FCSTD DOCUMENT  (FreeCAD 0.14R3692 (Git))
Label: Escornabot
License: The MIT License (MIT)
LicenseURL: http://opensource.org/licenses/MIT
objects: Part::Feature×46, Part::Mirroring×26, Sketcher::SketchObject×18, PartDesign::Pocket×14, App::DocumentObjectGroup×8, PartDesign::Pad×4, Part::Compound×4, Part::Fillet×2, PartDesign::Chamfer×2
note: 134 computed .brp shape members not serialized (recipe doc carries the construction recipe); baked Part::Feature solids carry a one-line shape summary decoded from their .brp

FEATURE [Sketcher::SketchObject] Sketch  label="UnderPlate_BaseSketch"
  sketch-geometry (25):
    g0: Circle CenterX=-37.5 CenterY=30 CenterZ=0 NormalX=0 NormalY=0 NormalZ=1 Radius=1.6
    g1: LineSegment StartX=-43.5 StartY=-45.5249 StartZ=0 EndX=-43.5 EndY=34.2012 EndZ=0
    g2: LineSegment StartX=-43.5 StartY=34.2012 StartZ=0 EndX=-19.3256 EndY=43 EndZ=0
    g3: LineSegment StartX=-19.3256 StartY=43 StartZ=0 EndX=19.3256 EndY=43 EndZ=0
    g4: LineSegment [constr] StartX=-37.5 StartY=30 StartZ=0 EndX=-39.5521 EndY=35.6382 EndZ=0
    g5: Circle CenterX=37.5 CenterY=30 CenterZ=0 NormalX=0 NormalY=0 NormalZ=1 Radius=1.6
    g6: Circle CenterX=-37.5 CenterY=-45 CenterZ=0 NormalX=0 NormalY=0 NormalZ=1 Radius=1.6
    g7: Circle CenterX=37.5 CenterY=-45 CenterZ=0 NormalX=0 NormalY=0 NormalZ=1 Radius=1.6
    g8: LineSegment [constr] StartX=-37.5 StartY=-45 StartZ=0 EndX=-43.4088 EndY=-46.0419 EndZ=0
    g9: LineSegment StartX=-37.556 StartY=-79.2349 StartZ=0 EndX=-43.5 EndY=-45.5249 EndZ=0
    g10: Circle CenterX=0 CenterY=0 CenterZ=0 NormalX=0 NormalY=0 NormalZ=1 Radius=9
    g11: LineSegment [constr] StartX=31.5 StartY=-74 StartZ=0 EndX=-31.5 EndY=-74 EndZ=0
    g12: LineSegment [constr] StartX=-31.5 StartY=-74 StartZ=0 EndX=-31.5 EndY=-16 EndZ=0
    g13: LineSegment [constr] StartX=-31.5 StartY=-16 StartZ=0 EndX=31.5 EndY=-16 EndZ=0
    g14: LineSegment [constr] StartX=31.5 StartY=-16 StartZ=0 EndX=31.5 EndY=-74 EndZ=0
    g15: LineSegment StartX=19.3256 StartY=43 StartZ=0 EndX=43.5 EndY=34.2012 EndZ=0
    g16: LineSegment StartX=43.5 StartY=34.2012 StartZ=0 EndX=43.5 EndY=-45.5249 EndZ=0
    g17: LineSegment StartX=43.5 StartY=-45.5249 StartZ=0 EndX=37.556 EndY=-79.2349 EndZ=0
    g18: LineSegment StartX=-37.556 StartY=-79.2349 StartZ=0 EndX=-19.3256 EndY=-92 EndZ=0
    g19: LineSegment StartX=-19.3256 StartY=-92 StartZ=0 EndX=19.3256 EndY=-92 EndZ=0
    g20: LineSegment StartX=37.556 StartY=-79.2349 StartZ=0 EndX=19.3256 EndY=-92 EndZ=0
    g21: LineSegment StartX=-31.5 StartY=-19 StartZ=0 EndX=31.5 EndY=-19 EndZ=0
    g22: LineSegment StartX=31.5 StartY=-19 StartZ=0 EndX=31.5 EndY=-71 EndZ=0
    g23: LineSegment StartX=31.5 StartY=-71 StartZ=0 EndX=-31.5 EndY=-71 EndZ=0
    g24: LineSegment StartX=-31.5 StartY=-71 StartZ=0 EndX=-31.5 EndY=-19 EndZ=0
  constraints (67):
    c: DistanceX(g-1,g0) = -37.5
    c: Radius(g0) = 1.6
    c: Coincident(g2,g1)
    c: Vertical(g1)
    c: DistanceX(g1,g0) = 6
    c: Coincident(g2,g3)
    c: Symmetric(g3,g2,g-2)
    c: Coincident(g4,g0)
    c: Distance(g4) = 6
    c: PointOnObject(g4,g2)
    c: Equal(g6,g7)
    c: Equal(g7,g5)
    c: Equal(g5,g0)
    c: Symmetric(g5,g0,g-2)
    c: Coincident(g8,g6)
    c: Distance(g8) = 6
    c: Coincident(g9,g1)
    c: PointOnObject(g8,g9)
    c: Radius(g10) = 9
    c: Coincident(g10,g-1)
    c: Coincident(g11,g12)
    c: Coincident(g12,g13)
    c: Coincident(g13,g14)
    c: Coincident(g14,g11)
    c: Horizontal(g11)
    c: Horizontal(g13)
    c: Vertical(g12)
    c: Vertical(g14)
    c: DistanceY(g14) = -58
    c: DistanceX(g13) = 63
    c: Angle(g9,g8) = 1.5708
    c: Angle(g4,g2) = 1.5708
    c: Angle(g2) = 0.349066
    c: Angle(g9) = 1.74533
    c: Symmetric(g12,g13,g-2)
    c: DistanceY(g-1,g13) = -16
    c: Symmetric(g15,g1,g-2)
    c: Coincident(g3,g15)
    c: Symmetric(g1,g16,g-2)
    c: Coincident(g16,g15)
    c: Symmetric(g17,g9,g-2)
    c: Coincident(g17,g16)
    c: Coincident(g9,g18)
    c: Angle(g18) = -0.610865
    c: Coincident(g19,g20)
    c: Coincident(g17,g20)
    c: Coincident(g18,g19)
    c: Symmetric(g19,g18,g-2)
    c: Equal(g19,g3)
    c: DistanceY(g11,g19) = -18
    c: Coincident(g21,g22)
    c: Coincident(g22,g23)
    c: Coincident(g23,g24)
    c: Coincident(g24,g21)
    c: Horizontal(g21)
    c: Horizontal(g23)
    c: Vertical(g22)
    c: Vertical(g24)
    c: PointOnObject(g21,g12)
    c: DistanceY(g23,g11) = -3
    c: DistanceY(g21,g12) = 3
    c: Symmetric(g21,g21,g-2)
    c: Symmetric(g7,g6,g-2)
    c: DistanceY(g0,g6) = -75
    c: DistanceY(g-1,g0) = 30
    c: DistanceX(g6,g1) = -6
    c: DistanceY(g-1,g2) = 43
FEATURE [PartDesign::Pad] Pad  label="UnderPlate_Base"
  Length = 3
  Length2 = 100
  Sketch = -> Sketch
  Type = 0
FEATURE [Sketcher::SketchObject] Sketch001  label="UnderPlate_BatteryRecessRearSketch"
  ExternalGeometry = -> [Pad]
  Placement = pos=(0,-19,0) rot=(1,0,0;1.5708rad)
  Support = -> Pad [Face11]
  sketch-geometry (4):
    g0: ArcOfCircle CenterX=-27.5 CenterY=5 CenterZ=0 NormalX=0 NormalY=0 NormalZ=1 Radius=4 StartAngle=1.5708 EndAngle=4.71239
    g1: ArcOfCircle CenterX=27.5 CenterY=5 CenterZ=0 NormalX=0 NormalY=0 NormalZ=1 Radius=4 StartAngle=4.71239 EndAngle=7.85398
    g2: LineSegment StartX=-27.5 StartY=1 StartZ=0 EndX=27.5 EndY=1 EndZ=0
    g3: LineSegment StartX=-27.5 StartY=9 StartZ=0 EndX=27.5 EndY=9 EndZ=0
  constraints (14):
    c: Tangent(g0,g2)
    c: Tangent(g0,g3)
    c: Tangent(g1,g2)
    c: Tangent(g1,g3)
    c: Coincident(g0,g3)
    c: Coincident(g0,g2)
    c: Coincident(g2,g1)
    c: Coincident(g3,g1)
    c: Horizontal(g2)
    c: Equal(g0,g1)
    c: Radius(g0) = 4
    c: DistanceX(g0,g-3) = -4
    c: Symmetric(g0,g1,g-2)
    c: DistanceY(g0,g-3) = -1
FEATURE [PartDesign::Pocket] Pocket  label="UnderPlate_BatteryRecessRear"
  Length = 3
  Sketch = -> Sketch001
  Type = 0
FEATURE [Sketcher::SketchObject] Sketch002  label="UnderPlate_BatteryRecessFrontSketch"
  ExternalGeometry = -> [Pocket]
  Placement = pos=(0,-71,0) rot=(0,0.707107,0.707107;3.14159rad)
  Support = -> Pocket [Face15]
  sketch-geometry (4):
    g0: ArcOfCircle CenterX=-27.5 CenterY=5 CenterZ=0 NormalX=0 NormalY=0 NormalZ=1 Radius=4 StartAngle=1.5708 EndAngle=4.71239
    g1: ArcOfCircle CenterX=27.5 CenterY=5 CenterZ=0 NormalX=0 NormalY=0 NormalZ=1 Radius=4 StartAngle=4.71239 EndAngle=7.85398
    g2: LineSegment StartX=-27.5 StartY=1 StartZ=0 EndX=27.5 EndY=1 EndZ=0
    g3: LineSegment StartX=-27.5 StartY=9 StartZ=0 EndX=27.5 EndY=9 EndZ=0
  constraints (13):
    c: Tangent(g0,g2)
    c: Tangent(g0,g3)
    c: Tangent(g1,g2)
    c: Tangent(g1,g3)
    c: Coincident(g0,g3)
    c: Coincident(g0,g2)
    c: Coincident(g2,g1)
    c: Coincident(g3,g1)
    c: Equal(g0,g1)
    c: Radius(g0) = 4
    c: Symmetric(g0,g1,g-2)
    c: DistanceY(g0,g-3) = -1
    c: DistanceX(g0,g-3) = -4
FEATURE [PartDesign::Pocket] Pocket001  label="UnderPlate_BatteryRecessFront"
  Length = 3
  Sketch = -> Sketch002
  Type = 0
FEATURE [Sketcher::SketchObject] Sketch003  label="UnderPlate_BallCasterCutOutSketch"
  ExternalGeometry = -> [Pocket001]
  Placement = pos=(0,0,3) rot=(0,0,1;0rad)
  Support = -> Pocket001 [Face5]
  sketch-geometry (14):
    g0: Circle CenterX=-15 CenterY=38 CenterZ=0 NormalX=0 NormalY=0 NormalZ=1 Radius=1.6
    g1: Circle CenterX=15 CenterY=38 CenterZ=0 NormalX=0 NormalY=0 NormalZ=1 Radius=1.6
    g2: LineSegment StartX=-10 StartY=43 StartZ=0 EndX=-10 EndY=38 EndZ=0
    g3: LineSegment StartX=-10 StartY=43 StartZ=0 EndX=10 EndY=43 EndZ=0
    g4: LineSegment StartX=10 StartY=43 StartZ=0 EndX=10 EndY=38 EndZ=0
    g5: ArcOfCircle CenterX=0 CenterY=38 CenterZ=0 NormalX=0 NormalY=0 NormalZ=1 Radius=10 StartAngle=3.14159 EndAngle=6.28319
    g6: ArcOfCircle CenterX=0 CenterY=-87 CenterZ=0 NormalX=0 NormalY=0 NormalZ=1 Radius=10 StartAngle=7.7e-11 EndAngle=3.14159
    g7: LineSegment StartX=10 StartY=-87 StartZ=0 EndX=10 EndY=-92 EndZ=0
    g8: LineSegment StartX=-10 StartY=-87 StartZ=0 EndX=-10 EndY=-92 EndZ=0
    g9: Circle CenterX=-15 CenterY=-87 CenterZ=0 NormalX=0 NormalY=0 NormalZ=1 Radius=1.6
    g10: Circle CenterX=15 CenterY=-87 CenterZ=0 NormalX=0 NormalY=0 NormalZ=1 Radius=1.6
    g11: LineSegment StartX=-10 StartY=-92 StartZ=0 EndX=10 EndY=-92 EndZ=0
    g12: LineSegment [constr] StartX=-15 StartY=38 StartZ=0 EndX=15 EndY=38 EndZ=0
    g13: LineSegment [constr] StartX=-15 StartY=-87 StartZ=0 EndX=15 EndY=-87 EndZ=0
  constraints (40):
    c: Radius(g0) = 1.6
    c: Equal(g0,g1)
    c: Symmetric(g1,g0,g-2)
    c: DistanceX(g1,g0) = -30
    c: Vertical(g2)
    c: Coincident(g3,g2)
    c: Vertical(g4)
    c: Coincident(g3,g4)
    c: Coincident(g5,g2)
    c: Coincident(g5,g4)
    c: Tangent(g4,g5)
    c: Tangent(g2,g5)
    c: Radius(g5) = 10
    c: PointOnObject(g5,g-2)
    c: PointOnObject(g6,g-2)
    c: Equal(g6,g5)
    c: Coincident(g6,g7)
    c: Vertical(g7)
    c: Tangent(g6,g7)
    c: Vertical(g8)
    c: Coincident(g6,g8)
    c: Tangent(g6,g8)
    c: Radius(g9) = 1.6
    c: Equal(g9,g10)
    c: Symmetric(g9,g10,g-2)
    c: DistanceX(g9,g10) = 30
    c: Coincident(g8,g11)
    c: Coincident(g7,g11)
    c: Coincident(g12,g1)
    c: Coincident(g12,g0)
    c: PointOnObject(g5,g12)
    c: Coincident(g13,g10)
    c: Coincident(g13,g9)
    c: PointOnObject(g6,g13)
    c: PointOnObject(g2,g-3)
    c: PointOnObject(g3,g-3)
    c: DistanceY(g0,g-3) = 5
    c: PointOnObject(g8,g-4)
    c: PointOnObject(g7,g-4)
    c: DistanceY(g9,g-4) = -5
FEATURE [PartDesign::Pocket] Pocket002  label="UnderPlate_BallCasterCutOut"
  Length = 5
  Sketch = -> Sketch003
  Type = 1
FEATURE [Sketcher::SketchObject] Sketch004  label="UnderPlate_MotorCutOutSketch"
  Placement = pos=(0,0,3) rot=(0,0,1;0rad)
  Support = -> Pocket002 [Face5]
  sketch-geometry (8):
    g0: LineSegment StartX=-43.5 StartY=9 StartZ=0 EndX=-23.5 EndY=9 EndZ=0
    g1: LineSegment StartX=-23.5 StartY=9 StartZ=0 EndX=-23.5 EndY=-9 EndZ=0
    g2: LineSegment StartX=-23.5 StartY=-9 StartZ=0 EndX=-43.5 EndY=-9 EndZ=0
    g3: LineSegment StartX=-43.5 StartY=-9 StartZ=0 EndX=-43.5 EndY=9 EndZ=0
    g4: LineSegment StartX=23.5 StartY=9 StartZ=0 EndX=43.5 EndY=9 EndZ=0
    g5: LineSegment StartX=43.5 StartY=9 StartZ=0 EndX=43.5 EndY=-9 EndZ=0
    g6: LineSegment StartX=43.5 StartY=-9 StartZ=0 EndX=23.5 EndY=-9 EndZ=0
    g7: LineSegment StartX=23.5 StartY=-9 StartZ=0 EndX=23.5 EndY=9 EndZ=0
  constraints (23):
    c: Coincident(g0,g1)
    c: Coincident(g1,g2)
    c: Coincident(g2,g3)
    c: Coincident(g3,g0)
    c: Horizontal(g0)
    c: Horizontal(g2)
    c: Vertical(g1)
    c: Vertical(g3)
    c: DistanceY(g1) = -18
    c: DistanceX(g2) = -20
    c: Symmetric(g0,g1,g-1)
    c: Coincident(g4,g5)
    c: Coincident(g5,g6)
    c: Coincident(g6,g7)
    c: Coincident(g7,g4)
    c: Horizontal(g4)
    c: Horizontal(g6)
    c: Vertical(g5)
    c: Vertical(g7)
    c: Equal(g2,g6)
    c: Equal(g7,g1)
    c: Symmetric(g1,g6,g-2)
    c: DistanceX(g0,g4) = 87
FEATURE [PartDesign::Pocket] Pocket003  label="UnderPlate_MotorCutOut"
  Length = 5
  Sketch = -> Sketch004
  Type = 1
FEATURE [Sketcher::SketchObject] Sketch005  label="UnderPlate_CutOutSketch"
  ExternalGeometry = -> [Pocket003]
  Placement = pos=(0,0,3) rot=(0,0,1;0rad)
  Support = -> Pocket003 [Face5]
  sketch-geometry (17):
    g0: LineSegment StartX=-31.5 StartY=32.1838 StartZ=0 EndX=-23.5 EndY=35.0956 EndZ=0
    g1: LineSegment StartX=-23.5 StartY=35.0956 StartZ=0 EndX=-23.5 EndY=15 EndZ=0
    g2: LineSegment StartX=-23.5 StartY=15 StartZ=0 EndX=-31.5 EndY=15 EndZ=0
    g3: LineSegment StartX=-31.5 StartY=15 StartZ=0 EndX=-31.5 EndY=32.1838 EndZ=0
    g4: LineSegment [constr] StartX=-31.5 StartY=32.1838 StartZ=0 EndX=-33.5521 EndY=37.822 EndZ=0
    g5: LineSegment StartX=23.5 StartY=35.0956 StartZ=0 EndX=31.5 EndY=32.1838 EndZ=0
    g6: LineSegment StartX=31.5 StartY=32.1838 StartZ=0 EndX=31.5 EndY=15 EndZ=0
    g7: LineSegment StartX=31.5 StartY=15 StartZ=0 EndX=23.5 EndY=15 EndZ=0
    g8: LineSegment StartX=23.5 StartY=15 StartZ=0 EndX=23.5 EndY=35.0956 EndZ=0
    g9: Circle [constr] CenterX=-15 CenterY=38 CenterZ=0 NormalX=0 NormalY=0 NormalZ=1 Radius=6.6
    g10: ArcOfCircle CenterX=0 CenterY=38 CenterZ=0 NormalX=0 NormalY=0 NormalZ=1 Radius=16 StartAngle=4.03512 EndAngle=5.38966
    g11: LineSegment StartX=-10.0267 StartY=25.5314 StartZ=0 EndX=-17.5 EndY=31.5411 EndZ=0
    g12: LineSegment StartX=10.0267 StartY=25.5314 StartZ=0 EndX=17.5 EndY=31.5411 EndZ=0
    g13: LineSegment StartX=-17.5 StartY=31.5411 StartZ=0 EndX=-17.5 EndY=15 EndZ=0
    g14: LineSegment StartX=-17.5 StartY=15 StartZ=0 EndX=17.5 EndY=15 EndZ=0
    g15: LineSegment StartX=17.5 StartY=15 StartZ=0 EndX=17.5 EndY=31.5411 EndZ=0
    g16: LineSegment [constr] StartX=-15 StartY=38 StartZ=0 EndX=0 EndY=38 EndZ=0
  constraints (48):
    c: Coincident(g0,g1)
    c: Coincident(g1,g2)
    c: Coincident(g2,g3)
    c: Coincident(g3,g0)
    c: Horizontal(g2)
    c: Vertical(g1)
    c: Vertical(g3)
    c: Coincident(g4,g0)
    c: Distance(g4) = 6
    c: DistanceX(g2) = -8
    c: DistanceY(g-1,g1) = 15
    c: Coincident(g5,g6)
    c: Coincident(g6,g7)
    c: Coincident(g7,g8)
    c: Coincident(g8,g5)
    c: Horizontal(g7)
    c: Vertical(g6)
    c: Vertical(g8)
    c: Symmetric(g7,g1,g-2)
    c: Symmetric(g5,g0,g-2)
    c: Symmetric(g5,g0,g-2)
    c: Radius(g9) = 6.6
    c: Coincident(g14,g15)
    c: Coincident(g12,g15)
    c: Coincident(g10,g12)
    c: Coincident(g10,g11)
    c: Coincident(g11,g13)
    c: Coincident(g13,g14)
    c: Tangent(g12,g10)
    c: Tangent(g11,g10)
    c: PointOnObject(g10,g-2)
    c: Symmetric(g13,g14,g-2)
    c: Vertical(g13)
    c: Vertical(g15)
    c: Tangent(g9,g11)
    c: DistanceX(g-1,g9) = -15
    c: DistanceX(g14) = 35
    c: DistanceY(g-1,g13) = 15
    c: Radius(g10) = 16
    c: Equal(g13,g15)
    c: Horizontal(g16)
    c: Coincident(g16,g10)
    c: Coincident(g16,g9)
    c: DistanceX(g1,g13) = 6
    c: PointOnObject(g4,g-3)
    c: Angle(g4,g-3) = 1.5708
    c: Parallel(g0,g-3)
    c: DistanceY(g-3,g9) = -5
FEATURE [PartDesign::Pocket] Pocket004  label="UnderPlate_CutOut"
  Length = 5
  Sketch = -> Sketch005
  Type = 1
FEATURE [Sketcher::SketchObject] Sketch007  label="UnderPlate_PenHolderScrewHolesSketch"
  Placement = pos=(0,0,3) rot=(0,0,1;0rad)
  Support = -> Pocket004 [Face5]
  sketch-geometry (2):
    g0: Circle CenterX=-16 CenterY=0 CenterZ=0 NormalX=0 NormalY=0 NormalZ=1 Radius=1.6
    g1: Circle CenterX=16 CenterY=0 CenterZ=0 NormalX=0 NormalY=0 NormalZ=1 Radius=1.6
  constraints (5):
    c: Radius(g0) = 1.6
    c: Symmetric(g0,g1,g-1)
    c: PointOnObject(g0,g-1)
    c: DistanceX(g0,g1) = 32
    c: Equal(g0,g1)
FEATURE [PartDesign::Pocket] Pocket006  label="UnderPlate_PenHolderScrewHoles"
  Length = 5
  Sketch = -> Sketch007
  Type = 1
FEATURE [Sketcher::SketchObject] Sketch010  label="MainPlate_BaseSketch"
  Placement = pos=(0,0,33) rot=(0,0,1;0rad)
  sketch-geometry (25):
    g0: Circle CenterX=-37.5 CenterY=30 CenterZ=0 NormalX=0 NormalY=0 NormalZ=1 Radius=1.6
    g1: LineSegment StartX=-40.6648 StartY=37.537 StartZ=0 EndX=-19.9572 EndY=30 EndZ=0
    g2: LineSegment StartX=-19.9572 StartY=30 StartZ=0 EndX=19.9572 EndY=30 EndZ=0
    g3: LineSegment [constr] StartX=-37.5 StartY=30 StartZ=0 EndX=-35.4479 EndY=35.6382 EndZ=0
    g4: Circle CenterX=37.5 CenterY=30 CenterZ=0 NormalX=0 NormalY=0 NormalZ=1 Radius=1.6
    g5: Circle CenterX=-37.5 CenterY=-45 CenterZ=0 NormalX=0 NormalY=0 NormalZ=1 Radius=1.6
    g6: Circle CenterX=37.5 CenterY=-45 CenterZ=0 NormalX=0 NormalY=0 NormalZ=1 Radius=1.6
    g7: Circle CenterX=0 CenterY=0 CenterZ=0 NormalX=0 NormalY=0 NormalZ=1 Radius=9
    g8: LineSegment StartX=19.9572 StartY=30 StartZ=0 EndX=40.6648 EndY=37.537 EndZ=0
    g9: LineSegment StartX=-42.8166 StartY=-49.45 StartZ=0 EndX=-19.9572 EndY=-57.7701 EndZ=0
    g10: LineSegment StartX=-19.9572 StartY=-57.7701 StartZ=0 EndX=19.9572 EndY=-57.7701 EndZ=0
    g11: LineSegment StartX=42.8166 StartY=-49.45 StartZ=0 EndX=19.9572 EndY=-57.7701 EndZ=0
    g12: LineSegment [constr] StartX=-37.5 StartY=-45 StartZ=0 EndX=-39.5521 EndY=-50.6382 EndZ=0
    g13: LineSegment StartX=-47.5 StartY=22.5 StartZ=0 EndX=-47.5 EndY=-22.5 EndZ=0
    g14: LineSegment StartX=47.5 StartY=22.5 StartZ=0 EndX=47.5 EndY=-22.5 EndZ=0
    g15: LineSegment [constr] StartX=-42.9622 StartY=32.4829 StartZ=0 EndX=-37.5 EndY=30 EndZ=0
    g16: LineSegment StartX=-40.6648 StartY=37.537 StartZ=0 EndX=-47.5 EndY=22.5 EndZ=0
    g17: LineSegment StartX=-47.5 StartY=-22.5 StartZ=0 EndX=-42.8166 EndY=-49.45 EndZ=0
    g18: LineSegment [constr] StartX=-37.5 StartY=-45 StartZ=0 EndX=-43.4114 EndY=-46.0273 EndZ=0
    g19: LineSegment [constr] StartX=-37.5 StartY=30 StartZ=0 EndX=37.5 EndY=30 EndZ=0
    g20: LineSegment [constr] StartX=37.5 StartY=30 StartZ=0 EndX=37.5 EndY=-45 EndZ=0
    g21: LineSegment [constr] StartX=37.5 StartY=-45 StartZ=0 EndX=-37.5 EndY=-45 EndZ=0
    g22: LineSegment [constr] StartX=-37.5 StartY=-45 StartZ=0 EndX=-37.5 EndY=30 EndZ=0
    g23: LineSegment StartX=40.6648 StartY=37.537 StartZ=0 EndX=47.5 EndY=22.5 EndZ=0
    g24: LineSegment StartX=47.5 StartY=-22.5 StartZ=0 EndX=42.8166 EndY=-49.45 EndZ=0
  constraints (63):
    c: Radius(g0) = 1.6
    c: Coincident(g1,g2)
    c: Symmetric(g2,g1,g-2)
    c: Coincident(g3,g0)
    c: Distance(g3) = 6
    c: PointOnObject(g3,g1)
    c: Radius(g7) = 9
    c: Coincident(g7,g-1)
    c: Angle(g3,g1) = 1.5708
    c: Angle(g1) = -0.349066
    c: Symmetric(g8,g1,g-2)
    c: Coincident(g2,g8)
    c: Symmetric(g11,g9,g-2)
    c: Coincident(g10,g11)
    c: Coincident(g9,g10)
    c: Symmetric(g10,g9,g-2)
    c: Coincident(g12,g5)
    c: PointOnObject(g12,g9)
    c: Symmetric(g13,g13,g-1)
    c: DistanceY(g13) = -45
    c: Symmetric(g13,g14,g-2)
    c: Symmetric(g14,g13,g-2)
    c: DistanceX(g14,g13) = -95
    c: Coincident(g15,g0)
    c: Coincident(g16,g13)
    c: Coincident(g16,g1)
    c: PointOnObject(g15,g16)
    c: Angle(g16,g15) = 1.5708
    c: Coincident(g17,g13)
    c: Coincident(g17,g9)
    c: PointOnObject(g18,g17)
    c: Coincident(g18,g5)
    c: Coincident(g19,g20)
    c: Coincident(g20,g21)
    c: Coincident(g21,g22)
    c: Coincident(g22,g19)
    c: Horizontal(g19)
    c: Horizontal(g21)
    c: Vertical(g20)
    c: Vertical(g22)
    c: Symmetric(g19,g19,g-2)
    c: DistanceX(g19) = 75
    c: DistanceY(g20) = -75
    c: DistanceY(g-1,g19) = 30
    c: Coincident(g14,g23)
    c: Coincident(g8,g23)
    c: Coincident(g11,g24)
    c: Coincident(g14,g24)
    c: Angle(g9,g12) = 1.5708
    c: Angle(g18,g17) = 1.5708
    c: Coincident(g4,g19)
    c: Coincident(g0,g19)
    c: Coincident(g5,g21)
    c: Coincident(g6,g20)
    c: Equal(g0,g4)
    c: Equal(g4,g6)
    c: Equal(g6,g5)
    c: Equal(g18,g12)
    c: Equal(g12,g15)
    c: Equal(g15,g3)
    c: Equal(g10,g2)
    c: Parallel(g9,g1)
    c: PointOnObject(g1,g19)
FEATURE [PartDesign::Pad] Pad002  label="MainPlate_Base"
  Length = 3
  Length2 = 100
  Placement = pos=(0,0,33) rot=(0,0,1;0rad)
  Sketch = -> Sketch010
  Type = 0
FEATURE [Sketcher::SketchObject] Sketch011  label="MainPlate_CutOutSketch"
  ExternalGeometry = -> [Pad002]
  Placement = pos=(0,0,36) rot=(0,0,1;0rad)
  Support = -> Pad002 [Face19]
  sketch-geometry (18):
    g0: LineSegment StartX=-23.5 StartY=5 StartZ=0 EndX=-23.5 EndY=24.9044 EndZ=0
    g1: LineSegment StartX=-23.5 StartY=24.9044 StartZ=0 EndX=-31.5 EndY=27.8162 EndZ=0
    g2: LineSegment StartX=-31.5 StartY=27.8162 StartZ=0 EndX=-31.5 EndY=5 EndZ=0
    g3: LineSegment StartX=-31.5 StartY=5 StartZ=0 EndX=-23.5 EndY=5 EndZ=0
    g4: LineSegment [constr] StartX=-31.5 StartY=27.8162 StartZ=0 EndX=-29.4479 EndY=33.4543 EndZ=0
    g5: LineSegment StartX=23.5 StartY=24.9044 StartZ=0 EndX=23.5 EndY=5 EndZ=0
    g6: LineSegment StartX=23.5 StartY=5 StartZ=0 EndX=31.5 EndY=5 EndZ=0
    g7: LineSegment StartX=31.5 StartY=5 StartZ=0 EndX=31.5 EndY=27.8162 EndZ=0
    g8: LineSegment StartX=31.5 StartY=27.8162 StartZ=0 EndX=23.5 EndY=24.9044 EndZ=0
    g9: LineSegment StartX=-31.5 StartY=-5 StartZ=0 EndX=-31.5 EndY=-47.1838 EndZ=0
    g10: LineSegment StartX=-31.5 StartY=-47.1838 StartZ=0 EndX=-23.5 EndY=-50.0956 EndZ=0
    g11: LineSegment StartX=-23.5 StartY=-50.0956 StartZ=0 EndX=-23.5 EndY=-5 EndZ=0
    g12: LineSegment StartX=-23.5 StartY=-5 StartZ=0 EndX=-31.5 EndY=-5 EndZ=0
    g13: LineSegment StartX=23.5 StartY=-5 StartZ=0 EndX=23.5 EndY=-50.0956 EndZ=0
    g14: LineSegment StartX=23.5 StartY=-50.0956 StartZ=0 EndX=31.5 EndY=-47.1838 EndZ=0
    g15: LineSegment StartX=31.5 StartY=-47.1838 StartZ=0 EndX=31.5 EndY=-5 EndZ=0
    g16: LineSegment StartX=31.5 StartY=-5 StartZ=0 EndX=23.5 EndY=-5 EndZ=0
    g17: LineSegment [constr] StartX=-31.5 StartY=-47.1838 StartZ=0 EndX=-33.5521 EndY=-52.822 EndZ=0
  constraints (48):
    c: Coincident(g0,g1)
    c: Coincident(g1,g2)
    c: Coincident(g2,g3)
    c: Coincident(g0,g3)
    c: Horizontal(g3)
    c: Vertical(g0)
    c: Vertical(g2)
    c: DistanceX(g3) = 8
    c: Coincident(g4,g1)
    c: Distance(g4) = 6
    c: DistanceY(g-1,g0) = 5
    c: Coincident(g5,g6)
    c: Coincident(g6,g7)
    c: Coincident(g7,g8)
    c: Coincident(g8,g5)
    c: Vertical(g5)
    c: Horizontal(g6)
    c: Coincident(g9,g10)
    c: Coincident(g10,g11)
    c: Coincident(g11,g12)
    c: Coincident(g12,g9)
    c: Vertical(g11)
    c: Horizontal(g12)
    c: Coincident(g13,g14)
    c: Coincident(g14,g15)
    c: Coincident(g13,g16)
    c: Coincident(g15,g16)
    c: Symmetric(g15,g9,g-2)
    c: Symmetric(g14,g9,g-2)
    c: Symmetric(g13,g10,g-2)
    c: Vertical(g13)
    c: Horizontal(g16)
    c: Vertical(g9)
    c: Vertical(g7)
    c: Symmetric(g1,g7,g-2)
    c: Symmetric(g5,g0,g-2)
    c: Symmetric(g2,g6,g-2)
    c: Symmetric(g9,g2,g-1)
    c: Coincident(g9,g17)
    c: Equal(g17,g4)
    c: Equal(g12,g3)
    c: PointOnObject(g17,g-4)
    c: PointOnObject(g4,g-3)
    c: Angle(g4,g-3) = 1.5708
    c: Angle(g17,g-4) = 1.5708
    c: Parallel(g-3,g1)
    c: Parallel(g10,g-4)
    c: DistanceX(g2,g6) = 63
FEATURE [PartDesign::Pocket] Pocket007002  label="MainPlate_CutOut"
  Length = 5
  Placement = pos=(0,0,33) rot=(0,0,1;0rad)
  Sketch = -> Sketch011
  Type = 1
FEATURE [Sketcher::SketchObject] Sketch012  label="MainPlate_BracketMountingScrewHolesSketch"
  Placement = pos=(0,0,36) rot=(0,0,1;0rad)
  Support = -> Pocket007002 [Face5]
  sketch-geometry (4):
    g0: Circle CenterX=-36.5 CenterY=17.5 CenterZ=0 NormalX=0 NormalY=0 NormalZ=1 Radius=1.6
    g1: Circle CenterX=-36.5 CenterY=-17.5 CenterZ=0 NormalX=0 NormalY=0 NormalZ=1 Radius=1.6
    g2: Circle CenterX=36.5 CenterY=17.5 CenterZ=0 NormalX=0 NormalY=0 NormalZ=1 Radius=1.6
    g3: Circle CenterX=36.5 CenterY=-17.5 CenterZ=0 NormalX=0 NormalY=0 NormalZ=1 Radius=1.6
  constraints (9):
    c: Radius(g0) = 1.6
    c: DistanceY(g-1,g0) = 17.5
    c: Equal(g3,g1)
    c: Equal(g1,g2)
    c: Equal(g2,g0)
    c: Symmetric(g2,g0,g-2)
    c: Symmetric(g0,g1,g-1)
    c: Symmetric(g1,g3,g-2)
    c: DistanceX(g0,g2) = 73
FEATURE [PartDesign::Pocket] Pocket007003  label="MainPlate_BracketMountingScrewHoles"
  Length = 5
  Placement = pos=(0,0,33) rot=(0,0,1;0rad)
  Sketch = -> Sketch012
  Type = 1
FEATURE [Part::Fillet] Fillet001  label="UnderPlate_RoundedCorners"
  Base = -> Pocket006
  Edges = 23 edges: [Edge1 r=6,Edge129 r=1,Edge130 r=1,Edge134 r=1,Edge136 r=1,Edge137 r=1,Edge138 r=1,Edge139 r=1,Edge140 r=1,Edge141 r=1,Edge142 r=1,Edge143 r=1,Edge144 r=1,Edge145 r=1,Edge147 r=1,Edge148 r=1,Edge152 r=6,Edge153 r=6,Edge156 r=1,Edge157 r=1,Edge162 r=1,Edge164 r=6,Edge166 r=1]
FEATURE [Sketcher::SketchObject] Sketch015  label="MainPlate_BracketMountingHeadHolesSketch"
  ExternalGeometry = -> [Pocket007003]
  Placement = pos=(0,0,36) rot=(0,0,1;0rad)
  Support = -> Pocket007003 [Face5]
  sketch-geometry (4):
    g0: Circle CenterX=-36.5 CenterY=17.5 CenterZ=0 NormalX=0 NormalY=0 NormalZ=1 Radius=2.95
    g1: Circle CenterX=36.5 CenterY=17.5 CenterZ=0 NormalX=0 NormalY=0 NormalZ=1 Radius=2.95
    g2: Circle CenterX=36.5 CenterY=-17.5 CenterZ=0 NormalX=0 NormalY=0 NormalZ=1 Radius=2.95
    g3: Circle CenterX=-36.5 CenterY=-17.5 CenterZ=0 NormalX=0 NormalY=0 NormalZ=1 Radius=2.95
  constraints (8):
    c: Radius(g0) = 2.95
    c: Equal(g0,g3)
    c: Equal(g3,g2)
    c: Equal(g2,g1)
    c: Symmetric(g0,g3,g-1)
    c: Symmetric(g0,g1,g-2)
    c: Symmetric(g0,g2,g-1)
    c: Coincident(g0,g-3)
FEATURE [PartDesign::Pocket] Pocket007004  label="MainPlate_BracketMountingHeadHoles"
  Length = 1
  Placement = pos=(0,0,33) rot=(0,0,1;0rad)
  Sketch = -> Sketch015
  Type = 0
FEATURE [Sketcher::SketchObject] Sketch016  label="MainPlate_ULN2003SpacerSketch"
  Placement = pos=(0,0,36) rot=(0,0,1;0rad)
  Support = -> Pocket007004 [Face5]
  sketch-geometry (10):
    g0: Circle CenterX=-12.875 CenterY=13.175 CenterZ=0 NormalX=0 NormalY=0 NormalZ=1 Radius=2.4
    g1: Circle CenterX=-43.125 CenterY=-13.175 CenterZ=0 NormalX=0 NormalY=0 NormalZ=1 Radius=2.4
    g2: Circle CenterX=-12.875 CenterY=-13.175 CenterZ=0 NormalX=0 NormalY=0 NormalZ=1 Radius=2.4
    g3: LineSegment [constr] StartX=-28 StartY=15.75 StartZ=0 EndX=-28 EndY=0 EndZ=0
    g4: LineSegment [constr] StartX=-28 StartY=0 StartZ=0 EndX=-45.55 EndY=0 EndZ=0
    g5: Circle CenterX=-43.125 CenterY=13.175 CenterZ=0 NormalX=0 NormalY=0 NormalZ=1 Radius=2.4
    g6: Circle CenterX=12.875 CenterY=13.175 CenterZ=0 NormalX=0 NormalY=0 NormalZ=1 Radius=2.4
    g7: Circle CenterX=12.875 CenterY=-13.175 CenterZ=0 NormalX=0 NormalY=0 NormalZ=1 Radius=2.4
    g8: Circle CenterX=43.125 CenterY=13.175 CenterZ=0 NormalX=0 NormalY=0 NormalZ=1 Radius=2.4
    g9: Circle CenterX=43.125 CenterY=-13.175 CenterZ=0 NormalX=0 NormalY=0 NormalZ=1 Radius=2.4
  constraints (24):
    c: Coincident(g3,g4)
    c: Horizontal(g4)
    c: Vertical(g3)
    c: DistanceX(g4) = -17.55
    c: DistanceY(g3) = -15.75
    c: DistanceX(g5,g3) = 15.125
    c: DistanceY(g5,g3) = -13.175
    c: Radius(g5) = 2.4
    c: Symmetric(g5,g0,g3)
    c: Symmetric(g1,g5,g4)
    c: Symmetric(g5,g2,g3)
    c: Equal(g5,g0)
    c: Equal(g0,g2)
    c: Equal(g2,g1)
    c: DistanceX(g-1,g3) = -28
    c: Symmetric(g6,g0,g-2)
    c: Symmetric(g8,g5,g-2)
    c: Symmetric(g9,g1,g-2)
    c: Symmetric(g7,g2,g-2)
    c: Equal(g7,g9)
    c: Equal(g9,g8)
    c: Equal(g8,g6)
    c: Equal(g6,g5)
    c: PointOnObject(g3,g-1)
FEATURE [PartDesign::Pad] Pad003  label="MainPlate_ULN2003Spacer"
  Length = 5
  Length2 = 100
  Placement = pos=(0,0,33) rot=(0,0,1;0rad)
  Sketch = -> Sketch016
  Type = 0
FEATURE [PartDesign::Chamfer] Chamfer  label="MainPlate_ULN2003SpacerChamfer"
  Base = -> Pad003 [Edge86,Edge89,Edge87,Edge83,Edge88,Edge84,Edge90,Edge85]
  Placement = pos=(0,0,33) rot=(0,0,1;0rad)
  Size = 1
FEATURE [Sketcher::SketchObject] Sketch017  label="MainPlate_ULN2003ScrewHolesSketch"
  ExternalGeometry = -> [Chamfer]
  Placement = pos=(0,0,36) rot=(0,0,1;0rad)
  Support = -> Chamfer [Face1]
  sketch-geometry (8):
    g0: Circle CenterX=-43.125 CenterY=13.175 CenterZ=0 NormalX=0 NormalY=0 NormalZ=1 Radius=1.4
    g1: Circle CenterX=-43.125 CenterY=-13.175 CenterZ=0 NormalX=0 NormalY=0 NormalZ=1 Radius=1.4
    g2: Circle CenterX=-12.875 CenterY=-13.175 CenterZ=0 NormalX=0 NormalY=0 NormalZ=1 Radius=1.4
    g3: Circle CenterX=12.875 CenterY=13.175 CenterZ=0 NormalX=0 NormalY=0 NormalZ=1 Radius=1.4
    g4: Circle CenterX=12.875 CenterY=-13.175 CenterZ=0 NormalX=0 NormalY=0 NormalZ=1 Radius=1.4
    g5: Circle CenterX=43.125 CenterY=13.175 CenterZ=0 NormalX=0 NormalY=0 NormalZ=1 Radius=1.4
    g6: Circle CenterX=43.125 CenterY=-13.175 CenterZ=0 NormalX=0 NormalY=0 NormalZ=1 Radius=1.4
    g7: Circle CenterX=-12.875 CenterY=13.175 CenterZ=0 NormalX=0 NormalY=0 NormalZ=1 Radius=1.4
  constraints (16):
    c: Coincident(g-3,g0)
    c: Symmetric(g1,g0,g-1)
    c: Symmetric(g2,g4,g-2)
    c: Symmetric(g1,g6,g-2)
    c: Symmetric(g5,g0,g-2)
    c: Radius(g0) = 1.4
    c: Coincident(g7,g-4)
    c: Equal(g0,g1)
    c: Equal(g1,g2)
    c: Equal(g2,g4)
    c: Equal(g4,g5)
    c: Equal(g5,g6)
    c: Equal(g6,g3)
    c: Equal(g3,g7)
    c: Symmetric(g2,g7,g-1)
    c: Symmetric(g7,g3,g-2)
FEATURE [PartDesign::Pocket] Pocket007005  label="MainPlate_ULN2003ScrewHoles"
  Length = 5
  Midplane = true
  Placement = pos=(0,0,33) rot=(0,0,1;0rad)
  Sketch = -> Sketch017
  Type = 1
FEATURE [Sketcher::SketchObject] Sketch013  label="MainPlate_BreadBoardOutSketch"
  ExternalGeometry = -> [Pocket007005]
  Placement = pos=(0,0,36) rot=(0,0,1;0rad)
  Support = -> Pocket007005 [Face2]
  sketch-geometry (4):
    g0: LineSegment StartX=-18.25 StartY=-17 StartZ=0 EndX=18.25 EndY=-17 EndZ=0
    g1: LineSegment StartX=18.25 StartY=-17 StartZ=0 EndX=18.25 EndY=-57.7701 EndZ=0
    g2: LineSegment StartX=18.25 StartY=-57.7701 StartZ=0 EndX=-18.25 EndY=-57.7701 EndZ=0
    g3: LineSegment StartX=-18.25 StartY=-57.7701 StartZ=0 EndX=-18.25 EndY=-17 EndZ=0
  constraints (12):
    c: Coincident(g0,g1)
    c: Coincident(g1,g2)
    c: Coincident(g2,g3)
    c: Coincident(g3,g0)
    c: Horizontal(g0)
    c: Horizontal(g2)
    c: Vertical(g1)
    c: Vertical(g3)
    c: DistanceX(g2) = -36.5
    c: Symmetric(g1,g2,g-2)
    c: DistanceY(g-1,g0) = -17
    c: PointOnObject(g2,g-3)
FEATURE [PartDesign::Pad] Pad004  label="MainPlate_BreadBoardOut"
  Length = 2
  Length2 = 100
  Placement = pos=(0,0,33) rot=(0,0,1;0rad)
  Sketch = -> Sketch013
  Type = 0
FEATURE [Sketcher::SketchObject] Sketch014  label="MainPlate_BreadBoardInSketch"
  Placement = pos=(0,0,36) rot=(0,0,1;0rad)
  Support = -> Pad004 [Face2]
  sketch-geometry (4):
    g0: LineSegment StartX=-17.25 StartY=-18 StartZ=0 EndX=17.25 EndY=-18 EndZ=0
    g1: LineSegment StartX=17.25 StartY=-18 StartZ=0 EndX=17.25 EndY=-63.5 EndZ=0
    g2: LineSegment StartX=17.25 StartY=-63.5 StartZ=0 EndX=-17.25 EndY=-63.5 EndZ=0
    g3: LineSegment StartX=-17.25 StartY=-63.5 StartZ=0 EndX=-17.25 EndY=-18 EndZ=0
  constraints (12):
    c: Coincident(g2,g3)
    c: Coincident(g1,g2)
    c: Coincident(g0,g3)
    c: Coincident(g0,g1)
    c: Horizontal(g0)
    c: Horizontal(g2)
    c: Vertical(g1)
    c: Vertical(g3)
    c: Symmetric(g2,g1,g-2)
    c: DistanceX(g0) = 34.5
    c: DistanceY(g3) = 45.5
    c: DistanceY(g-1,g0) = -18
FEATURE [PartDesign::Pocket] Pocket007006  label="MainPlate_BreadBoardIn"
  Length = 4
  Midplane = true
  Placement = pos=(0,0,33) rot=(0,0,1;0rad)
  Sketch = -> Sketch014
  Type = 0
FEATURE [Sketcher::SketchObject] Sketch018  label="MainPlate_ExtraScrewHolesSketch"
  Placement = pos=(0,0,36) rot=(0,0,1;0rad)
  Support = -> Pocket007006 [Face2]
  sketch-geometry (8):
    g0: Circle CenterX=-37.5 CenterY=-30 CenterZ=0 NormalX=0 NormalY=0 NormalZ=1 Radius=1.6
    g1: Circle CenterX=37.5 CenterY=-30 CenterZ=0 NormalX=0 NormalY=0 NormalZ=1 Radius=1.6
    g2: ArcOfCircle CenterX=-16 CenterY=24 CenterZ=0 NormalX=0 NormalY=0 NormalZ=1 Radius=1.6 StartAngle=1.5708 EndAngle=4.7124
    g3: ArcOfCircle CenterX=16 CenterY=24 CenterZ=0 NormalX=0 NormalY=0 NormalZ=1 Radius=1.6 StartAngle=4.71239 EndAngle=7.85399
    g4: LineSegment StartX=-16 StartY=22.4 StartZ=0 EndX=16 EndY=22.4 EndZ=0
    g5: LineSegment StartX=-16 StartY=25.6 StartZ=0 EndX=16 EndY=25.6 EndZ=0
    g6: Circle CenterX=-16 CenterY=0 CenterZ=0 NormalX=0 NormalY=0 NormalZ=1 Radius=1.6
    g7: Circle CenterX=16 CenterY=0 CenterZ=0 NormalX=0 NormalY=0 NormalZ=1 Radius=1.6
  constraints (25):
    c: Symmetric(g0,g1,g-2)
    c: Equal(g1,g0)
    c: Tangent(g2,g4)
    c: Tangent(g2,g5)
    c: Tangent(g3,g4)
    c: Tangent(g3,g5)
    c: Coincident(g2,g5)
    c: Coincident(g2,g4)
    c: Coincident(g4,g3)
    c: Coincident(g5,g3)
    c: Horizontal(g4)
    c: Equal(g2,g3)
    c: Radius(g2) = 1.6
    c: DistanceX(g5) = 32
    c: Symmetric(g2,g3,g-2)
    c: Radius(g6) = 1.6
    c: PointOnObject(g6,g-1)
    c: DistanceX(g-1,g6) = -16
    c: PointOnObject(g7,g-1)
    c: Equal(g7,g6)
    c: Symmetric(g7,g6,g-2)
    c: DistanceX(g0,g1) = 75
    c: DistanceY(g-1,g0) = -30
    c: DistanceY(g-1,g2) = 24
    c: Radius(g0) = 1.6
FEATURE [PartDesign::Pocket] Pocket007007  label="MainPlate_ExtraScrewHoles"
  Length = 5
  Placement = pos=(0,0,33) rot=(0,0,1;0rad)
  Sketch = -> Sketch018
  Type = 1
FEATURE [Sketcher::SketchObject] Sketch019  label="UnderPlate_ExtraHolesSketch"
  ExternalGeometry = -> [Fillet001]
  Placement = pos=(0,0,3) rot=(0,0,1;0rad)
  Support = -> Fillet001 [Face5]
  sketch-geometry (5):
    g0: Circle CenterX=-37.5 CenterY=-30 CenterZ=0 NormalX=0 NormalY=0 NormalZ=1 Radius=1.6
    g1: Circle CenterX=37.5 CenterY=-30 CenterZ=0 NormalX=0 NormalY=0 NormalZ=1 Radius=1.6
    g2: Circle CenterX=-25 CenterY=-80.3668 CenterZ=0 NormalX=0 NormalY=0 NormalZ=1 Radius=1.6
    g3: Circle CenterX=25 CenterY=-80.3668 CenterZ=0 NormalX=0 NormalY=0 NormalZ=1 Radius=1.6
    g4: LineSegment [constr] StartX=-25 StartY=-80.3668 StartZ=0 EndX=-28.599 EndY=-85.5067 EndZ=0
  constraints (13):
    c: Radius(g0) = 1.6
    c: DistanceY(g-1,g0) = -30
    c: Symmetric(g1,g0,g-2)
    c: Equal(g1,g0)
    c: DistanceX(g1,g0) = -75
    c: Symmetric(g2,g3,g-2)
    c: Radius(g2) = 1.6
    c: Equal(g2,g3)
    c: Distance(g-3,g2) = 12
    c: Coincident(g4,g2)
    c: PointOnObject(g4,g-4)
    c: Angle(g-4,g4) = 1.5708
    c: DistanceX(g2,g3) = 50
FEATURE [PartDesign::Pocket] Pocket007008  label="UnderPlate_ExtraHoles"
  Length = 5
  Sketch = -> Sketch019
  Type = 1
FEATURE [PartDesign::Chamfer] Chamfer001  label="UnderPlatePrintingChamfer"
  Base = -> Pocket007008 [Edge5,Edge6,Edge7,Edge8,Edge9,Edge10,Edge11,Edge12,Edge13,Edge14,Edge15,Edge16,Edge17,Edge18,Edge19,Edge20,Edge21,Edge22,Edge23,Edge24,Edge25,Edge26,Edge27,Edge28,Edge29,Edge30,Edge31,Edge32,Edge33,Edge34,Edge35,Edge36,Edge37,Edge38,Edge39,Edge40,Edge41,Edge42,Edge43,Edge44,+52 more]
  Size = 0.5
FEATURE [Sketcher::SketchObject] Sketch020  label="MainPlate_ExtraHeadHolesSketch"
  Placement = pos=(0,0,36) rot=(0,0,1;0rad)
  Support = -> Pocket007007 [Face2]
  sketch-geometry (2):
    g0: Circle CenterX=-16 CenterY=0 CenterZ=0 NormalX=0 NormalY=0 NormalZ=1 Radius=2.95
    g1: Circle CenterX=16 CenterY=0 CenterZ=0 NormalX=0 NormalY=0 NormalZ=1 Radius=2.95
  constraints (6):
    c: PointOnObject(g0,g-1)
    c: Radius(g0) = 2.95
    c: PointOnObject(g1,g-1)
    c: Equal(g1,g0)
    c: Symmetric(g1,g0,g-1)
    c: DistanceX(g1,g0) = -32
FEATURE [PartDesign::Pocket] Pocket007009  label="MainPlate_ExtraHeadHoles"
  Length = 1
  Placement = pos=(0,0,33) rot=(0,0,1;0rad)
  Sketch = -> Sketch020
  Type = 0
FEATURE [Part::Fillet] Fillet  label="MainPlate_RoundedCorners"
  Base = -> Pocket007009
  Edges = 20 edges: [Edge62 r=6,Edge71 r=6,Edge73 r=6,Edge91 r=6,Edge109 r=1,Edge110 r=1,Edge112 r=1,Edge114 r=1,Edge117 r=1,Edge118 r=1,Edge120 r=1,Edge122 r=1,Edge125 r=1,Edge126 r=1,Edge128 r=1,Edge130 r=1,Edge133 r=1,Edge134 r=1,Edge136 r=1,Edge138 r=1]
FEATURE [Part::Feature] Chamfer002001  label="MainPlate"
  shape: bbox 95 x 93.77 x 8 mm, 208 faces (baked)
FEATURE [Part::Feature] Chamfer001001  label="UnderPlate"
  shape: bbox 87 x 135 x 3 mm, 184 faces (baked)
FEATURE [Part::Feature] Part__Feature  label="BatteryHolder4xAA"
  Placement = pos=(0,-45,17) rot=(0,1,0;3.14159rad)
  shape: bbox 63 x 58 x 16 mm, 8 faces (baked)
FEATURE [Part::Feature] Part__Feature001  label="Bracket_BatteryHolder-4xAA"
  Placement = pos=(0,-45,3) rot=(1,0,0;1.5708rad)
  shape: bbox 87 x 12 x 16 mm, 36 faces (baked)
FEATURE [Part::Feature] Part__Feature003  label="BallFront"
  shape: bbox 14.5 x 14.5 x 14.5 mm, 1 faces (baked)
FEATURE [Part::Feature] Part__Feature004  label="BallCaster_14.5mmFront"
  shape: bbox 40 x 19 x 14.4 mm, 28 faces (baked)
FEATURE [Part::Compound] Compound  label="BallCasterFront"
  Links = -> [Part__Feature004,Part__Feature003]
  Placement = pos=(0,-87,5) rot=(1,0,0;3.14159rad)
FEATURE [Part::Feature] Part__Feature005  label="BallRear"
  shape: bbox 14.5 x 14.5 x 14.5 mm, 1 faces (baked)
FEATURE [Part::Feature] Part__Feature006  label="BallCaster_14.5mmRear"
  shape: bbox 40 x 19 x 14.4 mm, 28 faces (baked)
FEATURE [Part::Compound] Compound001  label="BallCasterRear"
  Links = -> [Part__Feature006,Part__Feature005]
  Placement = pos=(0,38,5) rot=(1,0,0;3.14159rad)
FEATURE [Part::Feature] Part__Feature007  label="PlateSpacer_28mmFrontRight"
  Placement = pos=(-37.5,-45,19) rot=(1,0,0;1.5708rad)
  shape: bbox 6.928 x 6 x 28 mm, 12 faces (baked)
FEATURE [Part::Feature] Part__Feature008  label="PlateSpacer_28mmFrontLeft"
  Placement = pos=(37.5,-45,19) rot=(1,0,0;1.5708rad)
  shape: bbox 6.928 x 6 x 28 mm, 12 faces (baked)
FEATURE [Part::Feature] Part__Feature009  label="PlateSpacer_30mmRearRight"
  Placement = pos=(-37.5,30,18) rot=(1,0,0;1.5708rad)
  shape: bbox 6.928 x 6 x 30 mm, 12 faces (baked)
FEATURE [Part::Feature] Part__Feature010  label="PlateSpacer_30mmRearLeft"
  Placement = pos=(37.5,30,18) rot=(1,0,0;1.5708rad)
  shape: bbox 6.928 x 6 x 30 mm, 12 faces (baked)
FEATURE [Part::Feature] Part__Feature019  label="DriverBoard_ULN2003Right"
  Placement = pos=(-28,0,41) rot=(0,0,1;0rad)
  shape: bbox 35.1 x 31.5 x 9.299 mm, 54 faces (baked)
FEATURE [Part::Feature] Part__Feature020  label="DriverBoard_ULN2003Left"
  Placement = pos=(28,0,41) rot=(0,0,1;3.14159rad)
  shape: bbox 35.1 x 31.5 x 9.299 mm, 54 faces (baked)
FEATURE [Part::Feature] Part__Feature062  label="Bracket_28BYJ-48Right"
  shape: bbox 16 x 45 x 40.75 mm, 556 faces (baked)
FEATURE [Part::Feature] Part__Feature063  label="Wheel_72mmRight"
  shape: bbox 6 x 72 x 72 mm, 30 faces (baked)
FEATURE [Part::Feature] Part__Feature064  label="ORing_72x3mmRight"
  shape: bbox 3 x 81.18 x 81.18 mm, 1 faces (baked)
FEATURE [Part::Feature] Part__Feature065  label="StepMotor_28BYJ-48Right"
  shape: bbox 28.55 x 42 x 44.13 mm, 425 faces (baked)
FEATURE [Part::Compound] Compound005  label="EngineCompoundRight"
  Links = -> [Part__Feature062,Part__Feature063,Part__Feature065,Part__Feature064]
  Placement = pos=(-36.5,0,33) rot=(0,0,1;3.14159rad)
FEATURE [Part::Feature] Part__Feature066  label="Bracket_28BYJ-48Left"
  shape: bbox 16 x 45 x 40.75 mm, 556 faces (baked)
FEATURE [Part::Feature] Part__Feature067  label="Wheel_72mmLeft"
  shape: bbox 6 x 72 x 72 mm, 30 faces (baked)
FEATURE [Part::Feature] Part__Feature068  label="ORing_72x3mmLeft"
  shape: bbox 3 x 81.18 x 81.18 mm, 1 faces (baked)
FEATURE [Part::Feature] Part__Feature069  label="StepMotor_28BYJ-48Left"
  shape: bbox 28.55 x 42 x 44.13 mm, 425 faces (baked)
FEATURE [Part::Compound] Compound006  label="EngineCompoundLeft"
  Links = -> [Part__Feature069,Part__Feature066,Part__Feature068,Part__Feature067]
  Placement = pos=(36.5,0,33) rot=(0,0,1;0rad)
FEATURE [Part::Feature] Part__Feature070  label="Board_ArduinoProMini"
  Placement = pos=(0,-63.5,34) rot=(0,0,1;0rad)
  shape: bbox 34.5 x 45.5 x 15.58 mm, 34 faces (baked)
FEATURE [Part::Feature] Part__Feature071  label="MainPlateSpacer_28mmRight"
  Placement = pos=(37.5,-30,50) rot=(0.935113,0.250563,0.250563;1.63783rad)
  shape: bbox 6 x 6.928 x 28 mm, 12 faces (baked)
FEATURE [Part::Feature] Part__Feature072  label="MainPlateSpacer_30mmRight"
  Placement = pos=(37.5,30,49) rot=(0.935113,0.250563,0.250563;1.63783rad)
  shape: bbox 6 x 6.928 x 30 mm, 12 faces (baked)
FEATURE [Part::Feature] Part__Feature071001  label="MainPlateSpacer_28mmLeft"
  Placement = pos=(-37.5,-30,50) rot=(0.935113,0.250563,0.250563;1.63783rad)
  shape: bbox 6 x 6.928 x 28 mm, 12 faces (baked)
FEATURE [Part::Feature] Part__Feature072001  label="MainPlateSpacer_30mmLeft"
  Placement = pos=(-37.5,30,49) rot=(0.935113,0.250563,0.250563;1.63783rad)
  shape: bbox 6 x 6.928 x 30 mm, 12 faces (baked)
FEATURE [Part::Feature] Part__Feature072002  label="Board_Keypad"
  Placement = pos=(-46.5,-10.9337,72.8034) rot=(-1,0,0;0.349066rad)
  shape: bbox 93 x 52.2 x 20.22 mm, 10 faces (baked)
FEATURE [App::DocumentObjectGroup] Grupo005  label="UpperPlate_Parts_Group"
  Group = -> [Part__Feature072002]
FEATURE [App::DocumentObjectGroup] Grupo004  label="UpperPlate_Group"
  Group = -> [Grupo005]
FEATURE [Part::Feature] Part__Feature072003  label="Bracket_Keypad-Left"
  Placement = pos=(0,0,36) rot=(0,0,1;0rad)
  shape: bbox 16 x 78 x 37.04 mm, 33 faces (baked)
FEATURE [Part::Feature] Part__Feature072004  label="Bracket_Keypad-Right"
  Placement = pos=(0,0,36) rot=(0,0,1;0rad)
  shape: bbox 16 x 78 x 37.04 mm, 33 faces (baked)
FEATURE [Part::Feature] Part__Feature072005001002  label="nut-000"
  shape: bbox 6.293 x 6.293 x 2.25 mm, 13 faces (baked)
FEATURE [Part::Feature] Part__Feature072005001003  label="bolt-000"
  shape: bbox 5.845 x 5.845 x 12.9 mm, 14 faces (baked)
FEATURE [Part::Feature] Part__Feature072005001003001  label="bolt-001"
  Placement = pos=(15,38,-5) rot=(0,0,1;0rad)
  shape: bbox 5.845 x 5.845 x 12.9 mm, 14 faces (baked)
FEATURE [Part::Feature] Part__Feature072005001002001  label="nut-001"
  Placement = pos=(15,38,-1) rot=(0,0,1;0rad)
  shape: bbox 6.293 x 6.293 x 2.25 mm, 13 faces (baked)
FEATURE [Part::Mirroring] Part__Mirroring  label="bolt-001 (Mirror #1)"
  Base = (0,0,0)
  Normal = (1,0,0)
  Source = -> Part__Feature072005001003001
FEATURE [Part::Mirroring] Part__Mirroring001  label="nut-001 (Mirror #2)"
  Base = (0,0,0)
  Normal = (1,0,0)
  Source = -> Part__Feature072005001002001
FEATURE [Part::Feature] Part__Feature072005001003002  label="bolt-002"
  Placement = pos=(15,-87,-5) rot=(0,0,1;0rad)
  shape: bbox 5.845 x 5.845 x 12.9 mm, 14 faces (baked)
FEATURE [Part::Feature] Part__Feature072005001002002  label="nut-002"
  Placement = pos=(15,-87,-1) rot=(0,0,1;0rad)
  shape: bbox 6.293 x 6.293 x 2.25 mm, 13 faces (baked)
FEATURE [Part::Mirroring] Part__Mirroring002  label="bolt-002 (Mirror #3)"
  Base = (0,0,0)
  Normal = (1,0,0)
  Source = -> Part__Feature072005001003002
FEATURE [Part::Mirroring] Part__Mirroring003  label="nut-002 (Mirror #4)"
  Base = (0,0,0)
  Normal = (1,0,0)
  Source = -> Part__Feature072005001002002
FEATURE [Part::Feature] Part__Feature072005001003003  label="bolt-003"
  Placement = pos=(37.5,30,10) rot=(0,1,0;3.14159rad)
  shape: bbox 5.845 x 5.845 x 12.9 mm, 14 faces (baked)
FEATURE [Part::Mirroring] Part__Mirroring004  label="bolt-003 (Mirror #5)"
  Base = (0,0,0)
  Normal = (1,0,0)
  Source = -> Part__Feature072005001003003
FEATURE [Part::Feature] Part__Feature072005001003004  label="bolt-004"
  Placement = pos=(37.5,-45,10) rot=(0,1,0;3.14159rad)
  shape: bbox 5.845 x 5.845 x 12.9 mm, 14 faces (baked)
FEATURE [Part::Mirroring] Part__Mirroring005  label="bolt-004 (Mirror #6)"
  Base = (0,0,0)
  Normal = (1,0,0)
  Source = -> Part__Feature072005001003004
FEATURE [App::DocumentObjectGroup] Grupo006  label="UnderPlate_Fasteners_Group"
  Group = -> [Part__Mirroring,Part__Mirroring001,Part__Mirroring002,Part__Mirroring003,Part__Mirroring004,Part__Mirroring005]
FEATURE [App::DocumentObjectGroup] Grupo003  label="UnderPlate_Parts_Group"
  Group = -> [Part__Feature,Part__Feature001,Compound,Compound001,Part__Feature007,Part__Feature008,Part__Feature009,Part__Feature010,Grupo006]
FEATURE [App::DocumentObjectGroup] Grupo002  label="UnderPlate_Group"
  Group = -> [Grupo003,Pad,Pocket,Pocket001,Pocket002,Pocket003,Pocket004,Pocket006,Fillet001,Pocket007008,Chamfer001,Chamfer001001]
FEATURE [Part::Feature] Part__Feature072005001003005  label="bolt-005"
  Placement = pos=(35.55,17.5,14.75) rot=(0,1,0;1.5708rad)
  shape: bbox 12.9 x 5.845 x 5.845 mm, 14 faces (baked)
FEATURE [Part::Mirroring] Part__Mirroring006  label="bolt-005 (Mirror #7)"
  Base = (0,0,0)
  Normal = (0,1,0)
  Source = -> Part__Feature072005001003005
FEATURE [Part::Mirroring] Part__Mirroring007  label="bolt-005 (Mirror #8)"
  Base = (0,0,0)
  Normal = (1,0,0)
  Source = -> Part__Feature072005001003005
FEATURE [Part::Mirroring] Part__Mirroring008  label="bolt-005 (Mirror #9)"
  Base = (0,0,0)
  Normal = (1,0,0)
  Source = -> Part__Mirroring006
FEATURE [Part::Feature] Part__Feature072005001002003  label="nut-003"
  Placement = pos=(41.95,17.5,14.75) rot=(0,1,0;1.5708rad)
  shape: bbox 2.25 x 6.293 x 6.293 mm, 13 faces (baked)
FEATURE [Part::Mirroring] Part__Mirroring009  label="nut-003 (Mirror #10)"
  Base = (0,0,0)
  Normal = (0,1,0)
  Source = -> Part__Feature072005001002003
FEATURE [Part::Mirroring] Part__Mirroring010  label="nut-003 (Mirror #11)"
  Base = (0,0,0)
  Normal = (1,0,0)
  Source = -> Part__Feature072005001002003
FEATURE [Part::Mirroring] Part__Mirroring011  label="nut-003 (Mirror #12)"
  Base = (0,0,0)
  Normal = (1,0,0)
  Source = -> Part__Mirroring009
FEATURE [Part::Feature] Part__Feature072005001003006  label="bolt-006"
  Placement = pos=(36.5,17.5,25) rot=(0,0,1;0rad)
  shape: bbox 5.845 x 5.845 x 12.9 mm, 14 faces (baked)
FEATURE [Part::Feature] Part__Feature072005001002004  label="nut-004"
  Placement = pos=(36.5,17.5,27.825) rot=(0,0,1;0rad)
  shape: bbox 6.293 x 6.293 x 2.25 mm, 13 faces (baked)
FEATURE [Part::Mirroring] Part__Mirroring012  label="bolt-006 (Mirror #13)"
  Base = (0,0,0)
  Normal = (0,1,0)
  Source = -> Part__Feature072005001003006
FEATURE [Part::Mirroring] Part__Mirroring013  label="nut-004 (Mirror #14)"
  Base = (0,0,0)
  Normal = (0,1,0)
  Source = -> Part__Feature072005001002004
FEATURE [Part::Mirroring] Part__Mirroring014  label="bolt-006 (Mirror #15)"
  Base = (0,0,0)
  Normal = (1,0,0)
  Source = -> Part__Feature072005001003006
FEATURE [Part::Mirroring] Part__Mirroring015  label="nut-004 (Mirror #16)"
  Base = (0,0,0)
  Normal = (1,0,0)
  Source = -> Part__Feature072005001002004
FEATURE [Part::Mirroring] Part__Mirroring016  label="bolt-006 (Mirror #17)"
  Base = (0,0,0)
  Normal = (1,0,0)
  Source = -> Part__Mirroring012
FEATURE [Part::Mirroring] Part__Mirroring017  label="nut-004 (Mirror #18)"
  Base = (0,0,0)
  Normal = (1,0,0)
  Source = -> Part__Mirroring013
FEATURE [Part::Feature] Part__Feature072005001003007  label="bolt-007"
  Placement = pos=(43.125,13.175,32.5) rot=(0,0,1;0rad)
  shape: bbox 5.845 x 5.845 x 12.9 mm, 14 faces (baked)
FEATURE [Part::Feature] Part__Feature072005001003007001  label="bolt-008"
  Placement = pos=(12.875,-13.175,32.5) rot=(0,0,1;0rad)
  shape: bbox 5.845 x 5.845 x 12.9 mm, 14 faces (baked)
FEATURE [Part::Mirroring] Part__Mirroring018  label="bolt-007 (Mirror #19)"
  Base = (0,0,0)
  Normal = (1,0,0)
  Source = -> Part__Feature072005001003007
FEATURE [Part::Mirroring] Part__Mirroring019  label="bolt-008 (Mirror #20)"
  Base = (0,0,0)
  Normal = (1,0,0)
  Source = -> Part__Feature072005001003007001
FEATURE [Part::Feature] Part__Feature072005001003007002  label="bolt-009"
  Placement = pos=(37.5,30,28) rot=(0,0,1;0rad)
  shape: bbox 5.845 x 5.845 x 12.9 mm, 14 faces (baked)
FEATURE [Part::Feature] Part__Feature072005001002005  label="nut-005"
  Placement = pos=(37.5,30,31.875) rot=(0,0,1;0rad)
  shape: bbox 6.293 x 6.293 x 2.25 mm, 13 faces (baked)
FEATURE [Part::Mirroring] Part__Mirroring020  label="bolt-009 (Mirror #21)"
  Base = (0,0,0)
  Normal = (0,1,0)
  Source = -> Part__Feature072005001003007002
FEATURE [Part::Mirroring] Part__Mirroring021  label="nut-005 (Mirror #22)"
  Base = (0,0,0)
  Normal = (0,1,0)
  Source = -> Part__Feature072005001002005
FEATURE [Part::Mirroring] Part__Mirroring022  label="bolt-009 (Mirror #23)"
  Base = (0,0,0)
  Normal = (1,0,0)
  Source = -> Part__Feature072005001003007002
FEATURE [Part::Mirroring] Part__Mirroring023  label="nut-005 (Mirror #24)"
  Base = (0,0,0)
  Normal = (1,0,0)
  Source = -> Part__Feature072005001002005
FEATURE [Part::Mirroring] Part__Mirroring024  label="bolt-009 (Mirror #25)"
  Base = (0,0,0)
  Normal = (1,0,0)
  Source = -> Part__Mirroring020
FEATURE [Part::Mirroring] Part__Mirroring025  label="nut-005 (Mirror #26)"
  Base = (0,0,0)
  Normal = (1,0,0)
  Source = -> Part__Mirroring021
FEATURE [App::DocumentObjectGroup] Grupo007  label="MainPlate_Fasteners_Group"
  Group = -> [Part__Mirroring007,Part__Mirroring008,Part__Mirroring010,Part__Mirroring011,Part__Mirroring014,Part__Mirroring015,Part__Mirroring016,Part__Mirroring017,Part__Mirroring018,Part__Mirroring019,Part__Mirroring022,Part__Mirroring023,Part__Mirroring024,Part__Mirroring025]
FEATURE [App::DocumentObjectGroup] Grupo001  label="MainPlate_Parts_Group"
  Group = -> [Part__Feature019,Part__Feature020,Compound005,Compound006,Part__Feature070,Part__Feature071,Part__Feature072,Part__Feature071001,Part__Feature072001,Part__Feature072003,Part__Feature072004,Grupo007]
FEATURE [App::DocumentObjectGroup] Grupo  label="MainPlate_Group"
  Group = -> [Grupo001,Pad002,Pocket007002,Pocket007003,Pocket007004,Pad003,Chamfer,Pocket007005,Pad004,Pocket007006,Pocket007007,Pocket007009,Fillet,Chamfer002001]
